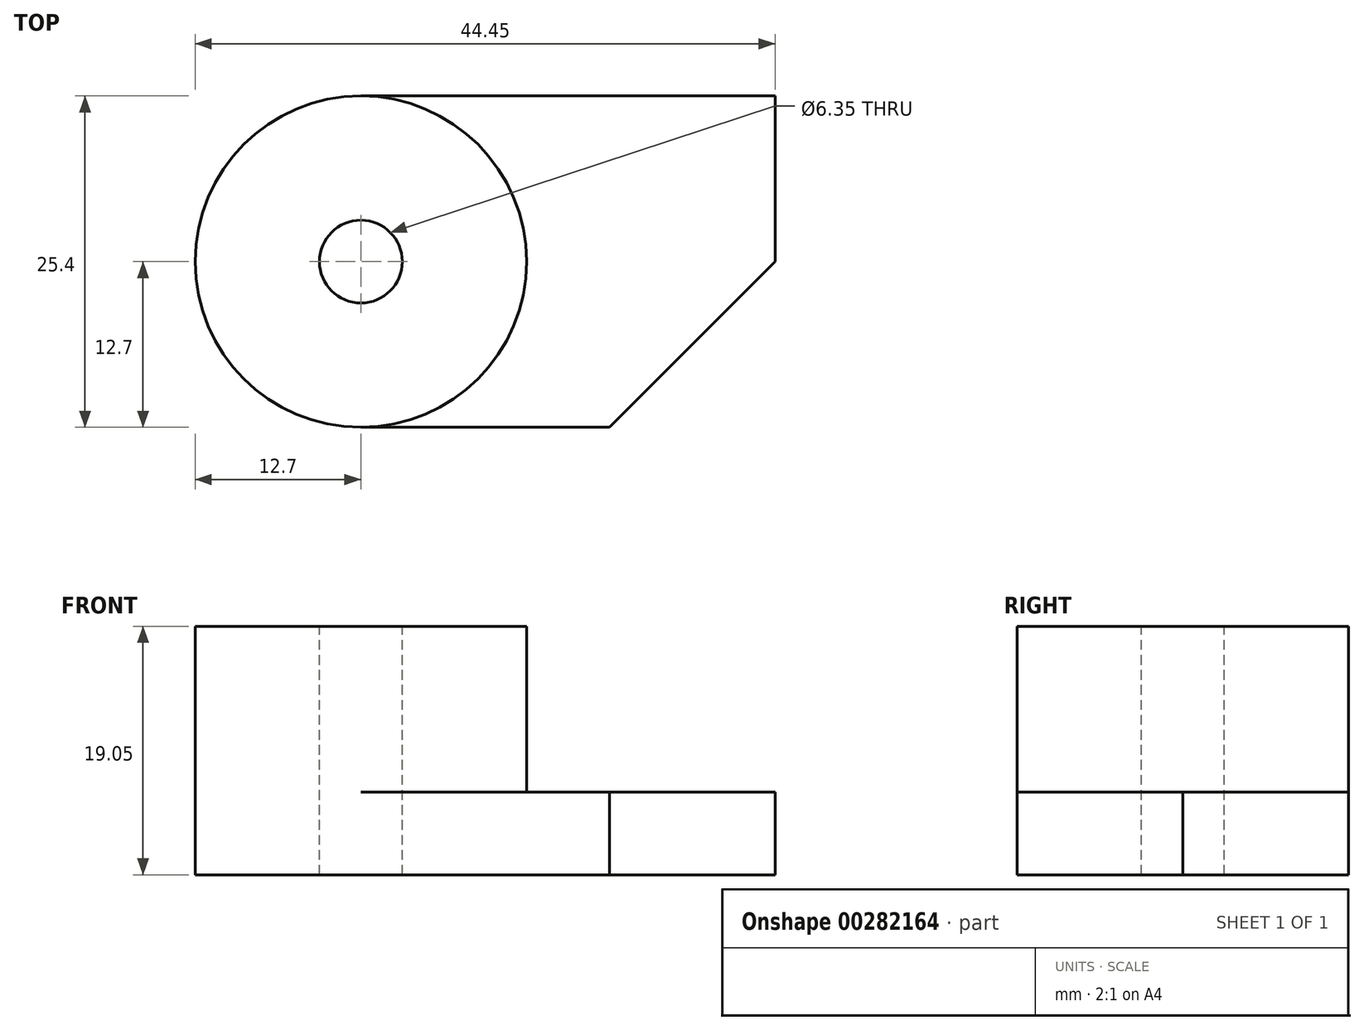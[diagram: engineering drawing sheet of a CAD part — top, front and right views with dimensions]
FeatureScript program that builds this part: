
annotation { "Feature Type Name" : "Feature", "Feature Type Description" : "" }
export const myFeature = defineFeature(function(context is Context, id is Id, definition is map)
    precondition{}
    {
        {
            var Q0;
            Q0=qCreatedBy(makeId("Right.planeOp"),FACE);
            var sketch = newSketch(context, id + "F0", { "sketchPlane" : qUnion([Q0])});
            skLineSegment(sketch, "E0", {"start": v(0, 0) * mm, "end": v(25.4, 0) * mm});
            skLineSegment(sketch, "E1", {"start": v(25.4, 0) * mm, "end": v(25.4, 6.35) * mm});
            skLineSegment(sketch, "E2", {"start": v(25.4, 6.35) * mm, "end": v(0, 6.35) * mm});
            skLineSegment(sketch, "E3", {"start": v(0, 6.35) * mm, "end": v(0, 0) * mm});
            skSolve(sketch);
        }
        {
            var Q0;
            Q0=makeQuery(id+"F0.imprint","IMPRINT",FACE,{"disambiguationData":[TD([[makeQuery(id+"F0.imprint","IMPRINT",EDGE,{"derivedFrom":sQuery(id+"F0.wireOp",EDGE,"E0")}),1.0]])]});
            extrude(context, id + "F1", {"entities" : qUnion([Q0]), "depth" : 44.45 * mm});
        }
        {
            var Q0;
            Q0=makeQuery(id+"F1.opExtrude","SWEPT_FACE",FACE,{"disambiguationData":[OSD([sQuery(id+"F0.wireOp",EDGE,"E2")])]});
            var sketch = newSketch(context, id + "F2", { "sketchPlane" : qUnion([Q0])});
            skLineSegment(sketch, "E4", {"start": v(44.45, 0) * mm, "end": v(44.45, 12.7) * mm});
            skLineSegment(sketch, "E5", {"start": v(44.45, 12.7) * mm, "end": v(31.75, 0) * mm});
            skLineSegment(sketch, "E6", {"start": v(31.75, 0) * mm, "end": v(44.45, 0) * mm});
            skSolve(sketch);
        }
        {
            var Q0;
            Q0=makeQuery(id+"F2.imprint","IMPRINT",FACE,{"disambiguationData":[TD([[makeQuery(id+"F2.imprint","IMPRINT",EDGE,{"derivedFrom":sQuery(id+"F2.wireOp",EDGE,"E4")}),-1.0]])]});
            extrude(context, id + "F3", {"entities" : qUnion([Q0]), "operationType" : NewBodyOperationType.REMOVE, "oppositeDirection" : true, "depth" : 6.35 * mm});
        }
        {
            var Q0;
            Q0=makeQuery(id+"F1.opExtrude","SWEPT_FACE",FACE,{"disambiguationData":[OSD([sQuery(id+"F0.wireOp",EDGE,"E2")])]});
            var sketch = newSketch(context, id + "F4", { "sketchPlane" : qUnion([Q0])});
            skCircle(sketch, "E7", {"center": v(12.7, 12.7) * mm, "radius": 12.7 * mm});
            skSolve(sketch);
        }
        {
            var Q0;
            {var subQ0=sQuery(id+"F4.wireOp",EDGE,"E7");var subQ1=sQuery(id+"F0.wireOp",EDGE,"E2");var subQ2=makeQuery(id+"F1.opExtrude","CAP_EDGE",EDGE,{"disambiguationData":[OSD([subQ1])],"isStart":true});var subQ3=makeQuery(id+"F4.imprint","INTERSECT",VERTEX,{"derivedFrom":[subQ2,subQ0]});Q0=makeQuery(id+"F4.imprint","IMPRINT",FACE,{"disambiguationData":[TD([[makeQuery(id+"F4.imprint","IMPRINT",EDGE,{"disambiguationData":[TD([[subQ3,-1.0]])],"derivedFrom":subQ0}),-1.0]])]});}
            var Q1;
            {var subQ0=sQuery(id+"F4.wireOp",EDGE,"E7");var subQ1=sQuery(id+"F0.wireOp",EDGE,"E2");var subQ2=makeQuery(id+"F1.opExtrude","CAP_EDGE",EDGE,{"disambiguationData":[OSD([subQ1])],"isStart":true});var subQ3=makeQuery(id+"F4.imprint","INTERSECT",VERTEX,{"derivedFrom":[subQ2,subQ0]});Q1=makeQuery(id+"F4.imprint","IMPRINT",FACE,{"disambiguationData":[TD([[makeQuery(id+"F4.imprint","IMPRINT",EDGE,{"disambiguationData":[TD([[subQ3,1.0]])],"derivedFrom":subQ0}),-1.0]])]});}
            extrude(context, id + "F5", {"entities" : qUnion([Q0, Q1]), "operationType" : NewBodyOperationType.REMOVE, "oppositeDirection" : true, "depth" : 6.35 * mm});
        }
        {
            var Q0;
            Q0 = qSketchRegion(id + "F4", true);
            extrude(context, id + "F6", {"entities" : qUnion([Q0]), "operationType" : NewBodyOperationType.ADD, "depth" : 12.7 * mm});
        }
        {
            var Q0;
            Q0=makeQuery(id+"F6.opExtrude","CAP_FACE",FACE,{"disambiguationData":[OSD([sQuery(id+"F4.wireOp",EDGE,"E7")])],"isStart":false});
            var sketch = newSketch(context, id + "F7", { "sketchPlane" : qUnion([Q0])});
            skCircle(sketch, "E8", {"center": v(12.7, 12.7) * mm, "radius": 3.18 * mm});
            skSolve(sketch);
        }
        {
            var Q0;
            Q0=makeQuery(id+"F7.imprint","IMPRINT",FACE,{"disambiguationData":[TD([[makeQuery(id+"F7.imprint","IMPRINT",EDGE,{"derivedFrom":sQuery(id+"F7.wireOp",EDGE,"E8")}),1.0]])]});
            extrude(context, id + "F8", {"entities" : qUnion([Q0]), "operationType" : NewBodyOperationType.REMOVE, "oppositeDirection" : true, "depth" : 19.05 * mm});
        }
    });
